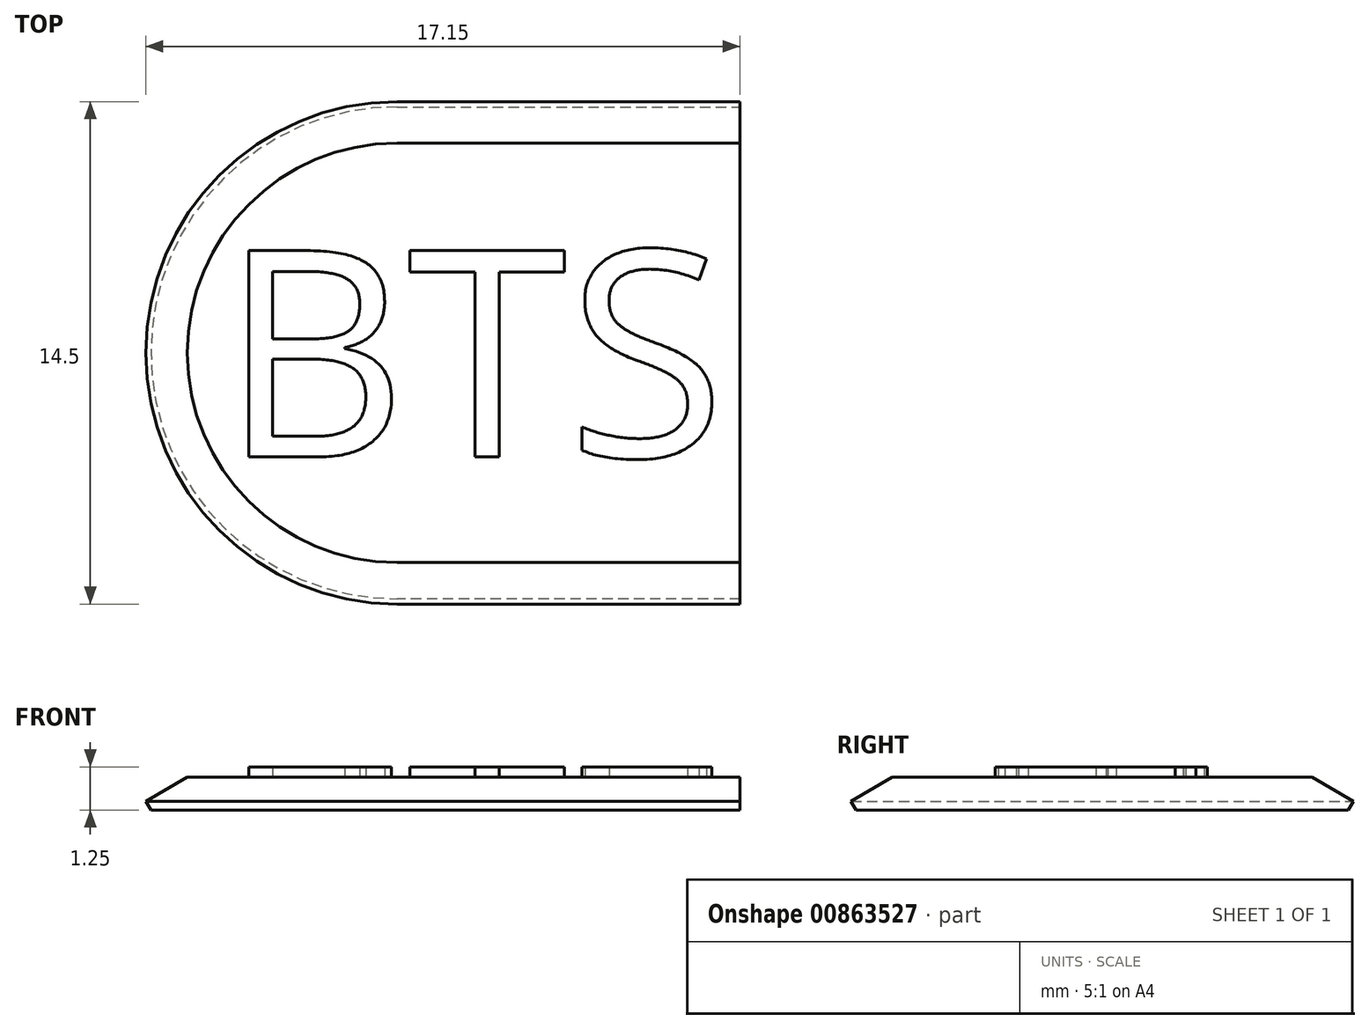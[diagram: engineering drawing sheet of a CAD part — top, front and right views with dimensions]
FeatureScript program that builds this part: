
annotation { "Feature Type Name" : "Feature", "Feature Type Description" : "" }
export const myFeature = defineFeature(function(context is Context, id is Id, definition is map)
    precondition{}
    {
        {
            var Q0;
            Q0=qCreatedBy(makeId("Top.planeOp"),FACE);
            var sketch = newSketch(context, id + "F0", { "sketchPlane" : qUnion([Q0])});
            skLineSegment(sketch, "E0", {"start": v(0, 0) * mm, "end": v(-9.9, 0) * mm});
            skLineSegment(sketch, "E1", {"start": v(0, 0) * mm, "end": v(0, 14.5) * mm, "construction": true});
            skArc(sketch, "E2", {"start": v(-9.9, 14.5) * mm, "mid": v(-17.15, 7.25) * mm, "end": v(-9.9, 0) * mm});
            skLineSegment(sketch, "E3", {"start": v(0, 14.5) * mm, "end": v(-9.9, 14.5) * mm});
            skPoint(sketch, "E4.orphan", {"position": v(0, 6.42) * mm});
            skSolve(sketch);
        }
        {
            var Q0;
            Q0=qCreatedBy(makeId("Right.planeOp"),FACE);
            var sketch = newSketch(context, id + "F1", { "sketchPlane" : qUnion([Q0])});
            skLineSegment(sketch, "E5", {"start": v(7.25, 0) * mm, "end": v(7.25, 0.95) * mm});
            skLineSegment(sketch, "E6", {"start": v(7.25, 0.95) * mm, "end": v(1.2, 0.95) * mm});
            skLineSegment(sketch, "E7", {"start": v(1.2, 0.95) * mm, "end": v(0, 0.26) * mm});
            skLineSegment(sketch, "E8", {"start": v(0, 0.26) * mm, "end": v(0.15, 0) * mm});
            skLineSegment(sketch, "E9", {"start": v(0.15, 0) * mm, "end": v(7.25, 0) * mm});
            skSolve(sketch);
        }
        {
            var Q0;
            Q0=makeQuery(id+"F1.imprint","IMPRINT",FACE,{"disambiguationData":[TD([[makeQuery(id+"F1.imprint","IMPRINT",EDGE,{"derivedFrom":sQuery(id+"F1.wireOp",EDGE,"E5")}),1.0]])]});
            var Q1;
            Q1=sQuery(id+"F0.wireOp",EDGE,"E0");
            var Q2;
            Q2=sQuery(id+"F0.wireOp",EDGE,"E2");
            var Q3;
            Q3=sQuery(id+"F0.wireOp",EDGE,"E3");
            sweep(context, id + "F2", {"profiles" : qUnion([Q0]), "path" : qUnion([Q1, Q2, Q3])});
        }
        {
            var Q0;
            Q0=makeQuery(id+"F2.opSweep","SWEPT_FACE",FACE,{"disambiguationData":[OSD([sQuery(id+"F0.wireOp",EDGE,"E0"),sQuery(id+"F1.wireOp",EDGE,"E6")])]});
            var sketch = newSketch(context, id + "F3", { "sketchPlane" : qUnion([Q0])});
            skText(sketch, "E10", { "text": "BTS", "fontName": "OpenSans-Regular.ttf"});
            skPoint(sketch, "E11", {"position": v(-0.27, 7.25) * mm});
            skLineSegment(sketch, "E12", {"start": v(-18.27, 7.25) * mm, "end": v(2.15, 7.25) * mm, "construction": true});
            const initialGuessF3  = {"E10": [-0.015, 0.00425, 1, 0, 0.006]};
            skSetInitialGuess(sketch, initialGuessF3);
            skSolve(sketch);
        }
        {
            var Q0;
            Q0 = qSketchRegion(id + "F3", true);
            extrude(context, id + "F4", {"entities" : qUnion([Q0]), "operationType" : NewBodyOperationType.ADD, "depth" : 0.3 * mm, "offsetDistance" : 25 * mm});
        }
    });
